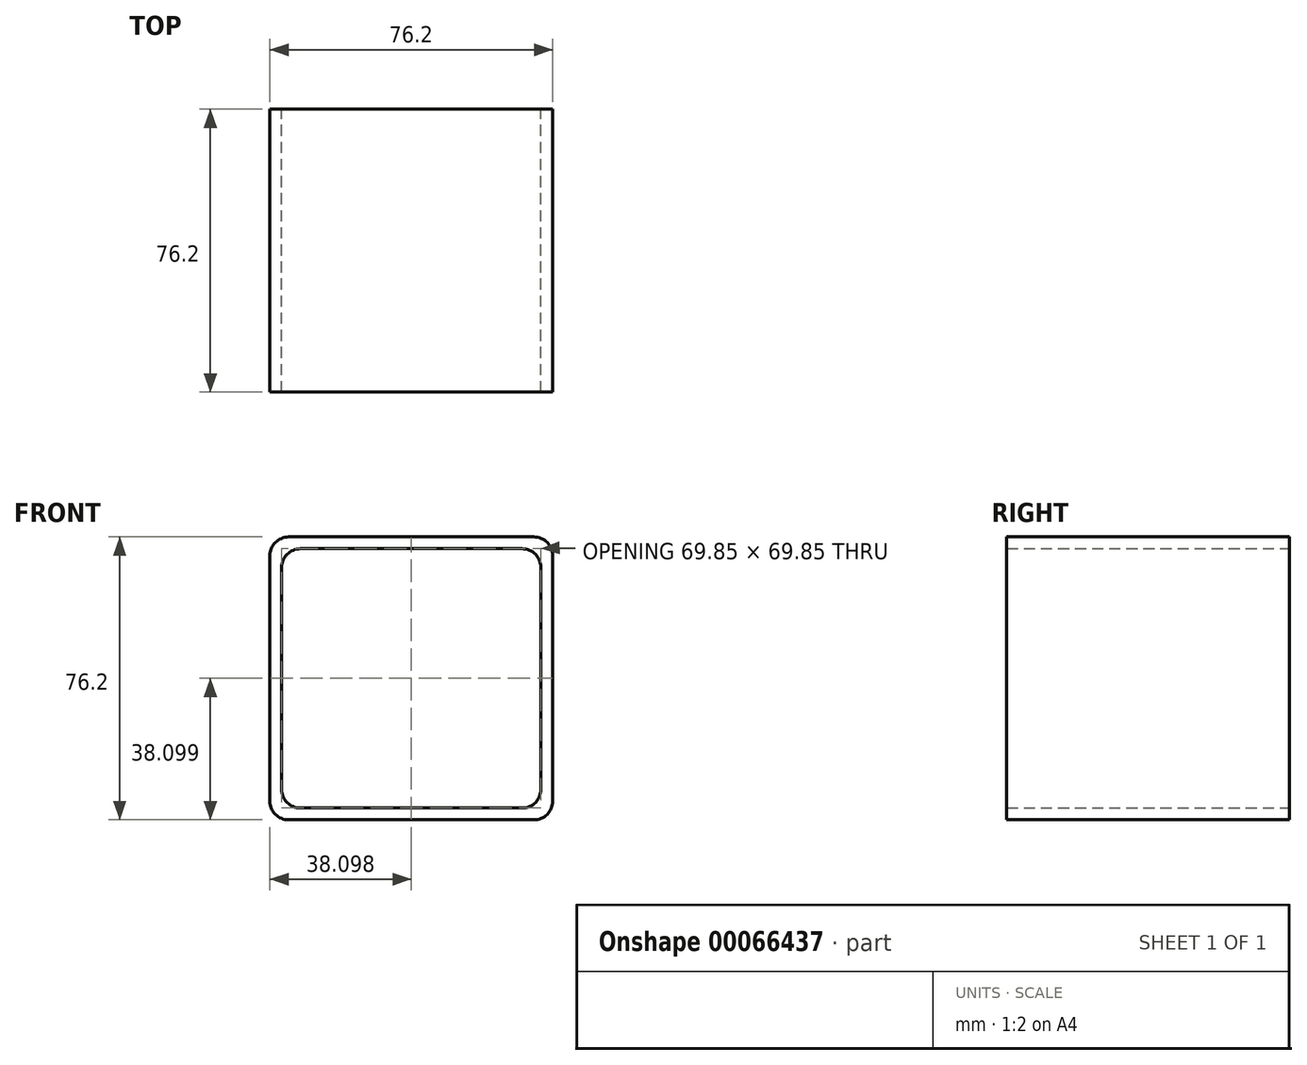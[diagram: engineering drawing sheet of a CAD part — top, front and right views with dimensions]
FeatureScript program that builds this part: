
annotation { "Feature Type Name" : "Feature", "Feature Type Description" : "" }
export const myFeature = defineFeature(function(context is Context, id is Id, definition is map)
    precondition{}
    {
        {
            var Q0;
            Q0=qCreatedBy(makeId("Front.planeOp"),FACE);
            var sketch = newSketch(context, id + "F0", { "sketchPlane" : qUnion([Q0])});
            skLineSegment(sketch, "E0.bottom", {"start": v(-31.03, 36.05) * mm, "end": v(45.17, 36.05) * mm});
            skLineSegment(sketch, "E0.top", {"start": v(-31.03, -40.15) * mm, "end": v(45.17, -40.15) * mm});
            skLineSegment(sketch, "E0.left", {"start": v(-31.03, 36.05) * mm, "end": v(-31.03, -40.15) * mm});
            skLineSegment(sketch, "E0.right", {"start": v(45.17, 36.05) * mm, "end": v(45.17, -40.15) * mm});
            skSolve(sketch);
        }
        {
            var Q0;
            Q0 = qSketchRegion(id + "F0", true);
            extrude(context, id + "F1", {"entities" : qUnion([Q0]), "depth" : 76.2 * mm});
        }
        {
            var Q0;
            Q0=makeQuery(id+"F1.opExtrude","CAP_FACE",FACE,{"disambiguationData":[OSD([sQuery(id+"F0.wireOp",EDGE,"E0.bottom"),sQuery(id+"F0.wireOp",EDGE,"E0.top"),sQuery(id+"F0.wireOp",EDGE,"E0.left"),sQuery(id+"F0.wireOp",EDGE,"E0.right")])],"isStart":false});
            var Q1;
            Q1=makeQuery(id+"F1.opExtrude","CAP_FACE",FACE,{"disambiguationData":[OSD([sQuery(id+"F0.wireOp",EDGE,"E0.bottom"),sQuery(id+"F0.wireOp",EDGE,"E0.top"),sQuery(id+"F0.wireOp",EDGE,"E0.left"),sQuery(id+"F0.wireOp",EDGE,"E0.right")])],"isStart":true});
            shell(context, id + "F2", {"entities" : qUnion([Q0, Q1]), "thickness" : 3.17 * mm});
        }
        {
            var Q0;
            Q0=makeQuery(id+"F2.opShell","OFFSET_EDGE",EDGE,{"disambiguationData":[OSD([sQuery(id+"F0.wireOp",EDGE,"E0.bottom"),sQuery(id+"F0.wireOp",EDGE,"E0.left")])]});
            var Q1;
            Q1=makeQuery(id+"F2.opShell","OFFSET_EDGE",EDGE,{"disambiguationData":[OSD([sQuery(id+"F0.wireOp",EDGE,"E0.top"),sQuery(id+"F0.wireOp",EDGE,"E0.right")])]});
            var Q2;
            Q2=makeQuery(id+"F2.opShell","OFFSET_EDGE",EDGE,{"disambiguationData":[OSD([sQuery(id+"F0.wireOp",EDGE,"E0.bottom"),sQuery(id+"F0.wireOp",EDGE,"E0.right")])]});
            var Q3;
            Q3=makeQuery(id+"F1.opExtrude","SWEPT_EDGE",EDGE,{"disambiguationData":[OSD([sQuery(id+"F0.wireOp",EDGE,"E0.top"),sQuery(id+"F0.wireOp",EDGE,"E0.left")])]});
            var Q4;
            Q4=makeQuery(id+"F1.opExtrude","SWEPT_EDGE",EDGE,{"disambiguationData":[OSD([sQuery(id+"F0.wireOp",EDGE,"E0.top"),sQuery(id+"F0.wireOp",EDGE,"E0.right")])]});
            var Q5;
            Q5=makeQuery(id+"F1.opExtrude","SWEPT_EDGE",EDGE,{"disambiguationData":[OSD([sQuery(id+"F0.wireOp",EDGE,"E0.bottom"),sQuery(id+"F0.wireOp",EDGE,"E0.right")])]});
            var Q6;
            Q6=makeQuery(id+"F1.opExtrude","SWEPT_EDGE",EDGE,{"disambiguationData":[OSD([sQuery(id+"F0.wireOp",EDGE,"E0.bottom"),sQuery(id+"F0.wireOp",EDGE,"E0.left")])]});
            var Q7;
            Q7=makeQuery(id+"F2.opShell","OFFSET_EDGE",EDGE,{"disambiguationData":[OSD([sQuery(id+"F0.wireOp",EDGE,"E0.top"),sQuery(id+"F0.wireOp",EDGE,"E0.left")])]});
            fillet(context, id + "F3", {"entities" : qUnion([Q0, Q1, Q2, Q3, Q4, Q5, Q6, Q7]), "radius" : 5.08 * mm, "tangentPropagation" : true, "allowEdgeOverflow" : false});
        }
    });
